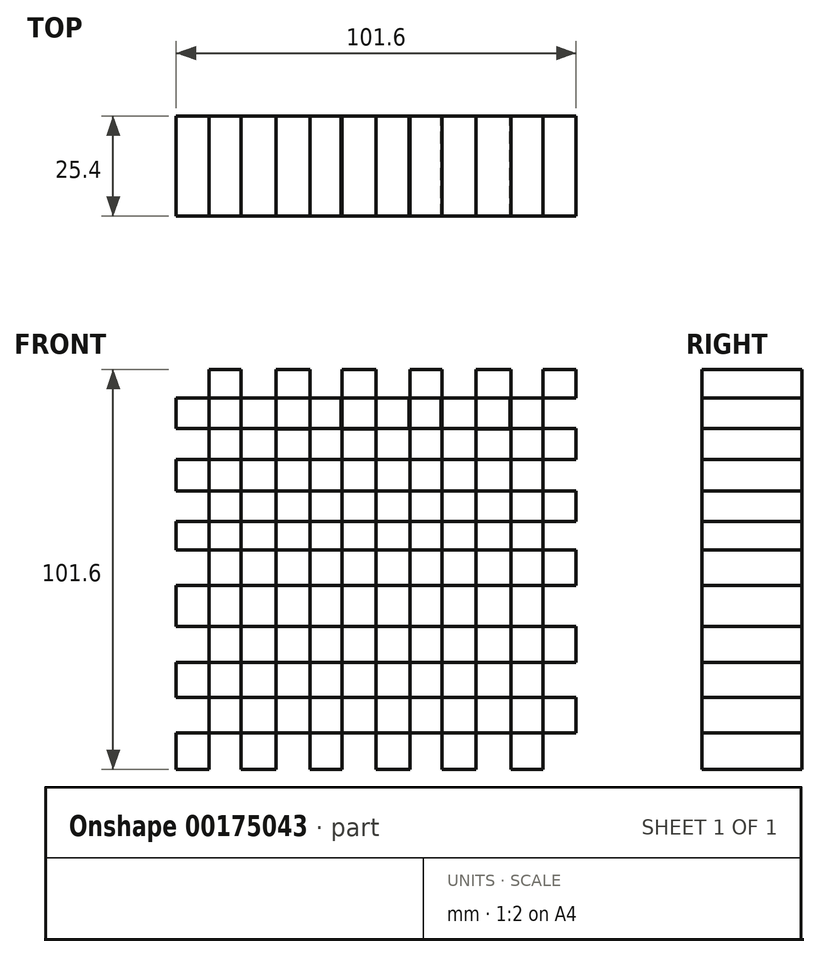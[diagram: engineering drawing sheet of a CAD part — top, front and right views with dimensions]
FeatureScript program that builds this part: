
annotation { "Feature Type Name" : "Feature", "Feature Type Description" : "" }
export const myFeature = defineFeature(function(context is Context, id is Id, definition is map)
    precondition{}
    {
        {
            var Q0;
            Q0=qCreatedBy(makeId("Front.planeOp"),FACE);
            var sketch = newSketch(context, id + "F0", { "sketchPlane" : qUnion([Q0])});
            skLineSegment(sketch, "E0.bottom", {"start": v(-50.8, 45.86) * mm, "end": v(0, 45.86) * mm});
            skLineSegment(sketch, "E0.top", {"start": v(-50.8, -55.74) * mm, "end": v(0, -55.74) * mm});
            skLineSegment(sketch, "E0.left", {"start": v(-50.8, 45.86) * mm, "end": v(-50.8, -55.74) * mm});
            skLineSegment(sketch, "E1", {"start": v(0, 45.86) * mm, "end": v(0, -55.74) * mm});
            skLineSegment(sketch, "E2", {"start": v(-34.3, 45.86) * mm, "end": v(-34.3, -55.74) * mm});
            skLineSegment(sketch, "E3", {"start": v(-16.76, 45.86) * mm, "end": v(-16.76, -55.74) * mm});
            skLineSegment(sketch, "E4", {"start": v(-25.4, 45.86) * mm, "end": v(-25.4, -55.74) * mm});
            skLineSegment(sketch, "E5", {"start": v(-42.42, 45.86) * mm, "end": v(-42.42, -55.74) * mm});
            skLineSegment(sketch, "E6", {"start": v(-8.64, 45.86) * mm, "end": v(-8.64, -55.74) * mm});
            skLineSegment(sketch, "E7", {"start": v(0, 0) * mm, "end": v(-50.8, 0) * mm});
            skLineSegment(sketch, "E8", {"start": v(-50.8, 23.07) * mm, "end": v(0, 23.07) * mm});
            skLineSegment(sketch, "E9", {"start": v(-50.8, -28.57) * mm, "end": v(0, -28.57) * mm});
            skLineSegment(sketch, "E10", {"start": v(-50.8, -9.03) * mm, "end": v(0, -9.03) * mm});
            skLineSegment(sketch, "E11", {"start": v(-50.8, -46.5) * mm, "end": v(0, -46.5) * mm});
            skLineSegment(sketch, "E12", {"start": v(-50.8, 30.83) * mm, "end": v(0, 30.83) * mm});
            skLineSegment(sketch, "E13", {"start": v(-50.8, 38.59) * mm, "end": v(0, 38.59) * mm});
            skLineSegment(sketch, "E14", {"start": v(-50.8, 15.04) * mm, "end": v(0, 15.04) * mm});
            skLineSegment(sketch, "E15", {"start": v(-50.8, 7.29) * mm, "end": v(0, 7.29) * mm});
            skLineSegment(sketch, "E16", {"start": v(-50.8, -19.47) * mm, "end": v(0, -19.47) * mm});
            skLineSegment(sketch, "E17", {"start": v(-50.8, -37.4) * mm, "end": v(0, -37.4) * mm});
            skLineSegment(sketch, "E18.MirrorCS", {"start": v(50.8, 45.86) * mm, "end": v(0, 45.86) * mm});
            skLineSegment(sketch, "E19.MirrorCS", {"start": v(50.8, 45.86) * mm, "end": v(50.8, -55.74) * mm});
            skLineSegment(sketch, "E20.MirrorCS", {"start": v(50.8, -55.74) * mm, "end": v(0, -55.74) * mm});
            skLineSegment(sketch, "E21.MirrorCS", {"start": v(42.42, 45.86) * mm, "end": v(42.42, -55.74) * mm});
            skLineSegment(sketch, "E22.MirrorCS", {"start": v(34.3, 45.86) * mm, "end": v(34.3, -55.74) * mm});
            skLineSegment(sketch, "E23.MirrorCS", {"start": v(25.4, 45.86) * mm, "end": v(25.4, -55.74) * mm});
            skLineSegment(sketch, "E24.MirrorCS", {"start": v(16.76, 45.86) * mm, "end": v(16.76, -55.74) * mm});
            skLineSegment(sketch, "E25.MirrorCS", {"start": v(8.64, 45.86) * mm, "end": v(8.64, -55.74) * mm});
            skLineSegment(sketch, "E26.MirrorCS", {"start": v(50.8, 38.59) * mm, "end": v(0, 38.59) * mm});
            skLineSegment(sketch, "E27.MirrorCS", {"start": v(50.8, 30.83) * mm, "end": v(0, 30.83) * mm});
            skLineSegment(sketch, "E28.MirrorCS", {"start": v(50.8, 23.07) * mm, "end": v(0, 23.07) * mm});
            skLineSegment(sketch, "E29.MirrorCS", {"start": v(50.8, 15.04) * mm, "end": v(0, 15.04) * mm});
            skLineSegment(sketch, "E30.MirrorCS", {"start": v(50.8, 7.29) * mm, "end": v(0, 7.29) * mm});
            skLineSegment(sketch, "E31.MirrorCS", {"start": v(0, 0) * mm, "end": v(50.8, 0) * mm});
            skLineSegment(sketch, "E32.MirrorCS", {"start": v(50.8, -9.03) * mm, "end": v(0, -9.03) * mm});
            skLineSegment(sketch, "E33.MirrorCS", {"start": v(50.8, -19.47) * mm, "end": v(0, -19.47) * mm});
            skLineSegment(sketch, "E34.MirrorCS", {"start": v(50.8, -28.57) * mm, "end": v(0, -28.57) * mm});
            skLineSegment(sketch, "E35.MirrorCS", {"start": v(50.8, -37.4) * mm, "end": v(0, -37.4) * mm});
            skLineSegment(sketch, "E36.MirrorCS", {"start": v(50.8, -46.5) * mm, "end": v(0, -46.5) * mm});
            skSolve(sketch);
        }
        {
            var Q0;
            {var subQ0=sQuery(id+"F0.wireOp",EDGE,"E0.left");var subQ1=sQuery(id+"F0.wireOp",EDGE,"E0.top");var subQ2=makeQuery(id+"F0.imprint","INTERSECT",VERTEX,{"derivedFrom":[subQ1,subQ0]});Q0=makeQuery(id+"F0.imprint","IMPRINT",FACE,{"disambiguationData":[TD([[makeQuery(id+"F0.imprint","IMPRINT",EDGE,{"disambiguationData":[TD([[subQ2,-1.0]])],"derivedFrom":subQ1}),1.0]])]});}
            var Q1;
            {var subQ0=sQuery(id+"F0.wireOp",EDGE,"E19.MirrorCS");var subQ1=sQuery(id+"F0.wireOp",EDGE,"E18.MirrorCS");var subQ2=makeQuery(id+"F0.imprint","INTERSECT",VERTEX,{"derivedFrom":[subQ1,subQ0]});Q1=makeQuery(id+"F0.imprint","IMPRINT",FACE,{"disambiguationData":[TD([[makeQuery(id+"F0.imprint","IMPRINT",EDGE,{"disambiguationData":[TD([[subQ2,-1.0]])],"derivedFrom":subQ1}),1.0]])]});}
            var Q2;
            {var subQ0=sQuery(id+"F0.wireOp",EDGE,"E2");var subQ1=sQuery(id+"F0.wireOp",EDGE,"E0.bottom");var subQ2=makeQuery(id+"F0.imprint","INTERSECT",VERTEX,{"derivedFrom":[subQ1,subQ0]});Q2=makeQuery(id+"F0.imprint","IMPRINT",FACE,{"disambiguationData":[TD([[makeQuery(id+"F0.imprint","IMPRINT",EDGE,{"disambiguationData":[TD([[subQ2,1.0]])],"derivedFrom":subQ1}),-1.0]])]});}
            var Q3;
            {var subQ0=sQuery(id+"F0.wireOp",EDGE,"E3");var subQ1=sQuery(id+"F0.wireOp",EDGE,"E0.bottom");var subQ2=makeQuery(id+"F0.imprint","INTERSECT",VERTEX,{"derivedFrom":[subQ1,subQ0]});Q3=makeQuery(id+"F0.imprint","IMPRINT",FACE,{"disambiguationData":[TD([[makeQuery(id+"F0.imprint","IMPRINT",EDGE,{"disambiguationData":[TD([[subQ2,1.0]])],"derivedFrom":subQ1}),-1.0]])]});}
            var Q4;
            {var subQ1=sQuery(id+"F0.wireOp",EDGE,"E0.bottom");var subQ3=sQuery(id+"F0.wireOp",EDGE,"E6");var subQ4=makeQuery(id+"F0.imprint","INTERSECT",VERTEX,{"derivedFrom":[subQ1,subQ3]});Q4=makeQuery(id+"F0.imprint","IMPRINT",FACE,{"disambiguationData":[TD([[makeQuery(id+"F0.imprint","IMPRINT",EDGE,{"disambiguationData":[TD([[subQ4,-1.0]])],"derivedFrom":subQ3}),1.0]])]});}
            var Q5;
            {var subQ0=sQuery(id+"F0.wireOp",EDGE,"E2");var subQ1=sQuery(id+"F0.wireOp",EDGE,"E0.top");var subQ2=makeQuery(id+"F0.imprint","INTERSECT",VERTEX,{"derivedFrom":[subQ1,subQ0]});Q5=makeQuery(id+"F0.imprint","IMPRINT",FACE,{"disambiguationData":[TD([[makeQuery(id+"F0.imprint","IMPRINT",EDGE,{"disambiguationData":[TD([[subQ2,-1.0]])],"derivedFrom":subQ1}),1.0]])]});}
            var Q6;
            {var subQ0=sQuery(id+"F0.wireOp",EDGE,"E3");var subQ1=sQuery(id+"F0.wireOp",EDGE,"E0.top");var subQ2=makeQuery(id+"F0.imprint","INTERSECT",VERTEX,{"derivedFrom":[subQ1,subQ0]});Q6=makeQuery(id+"F0.imprint","IMPRINT",FACE,{"disambiguationData":[TD([[makeQuery(id+"F0.imprint","IMPRINT",EDGE,{"disambiguationData":[TD([[subQ2,-1.0]])],"derivedFrom":subQ1}),1.0]])]});}
            var Q7;
            {var subQ0=sQuery(id+"F0.wireOp",EDGE,"E12");var subQ1=sQuery(id+"F0.wireOp",EDGE,"E0.left");var subQ2=makeQuery(id+"F0.imprint","INTERSECT",VERTEX,{"derivedFrom":[subQ1,subQ0]});Q7=makeQuery(id+"F0.imprint","IMPRINT",FACE,{"disambiguationData":[TD([[makeQuery(id+"F0.imprint","IMPRINT",EDGE,{"disambiguationData":[TD([[subQ2,1.0]])],"derivedFrom":subQ1}),1.0]])]});}
            var Q8;
            {var subQ0=sQuery(id+"F0.wireOp",EDGE,"E8");var subQ1=sQuery(id+"F0.wireOp",EDGE,"E0.left");var subQ2=makeQuery(id+"F0.imprint","INTERSECT",VERTEX,{"derivedFrom":[subQ1,subQ0]});Q8=makeQuery(id+"F0.imprint","IMPRINT",FACE,{"disambiguationData":[TD([[makeQuery(id+"F0.imprint","IMPRINT",EDGE,{"disambiguationData":[TD([[subQ2,-1.0]])],"derivedFrom":subQ1}),1.0]])]});}
            var Q9;
            {var subQ0=sQuery(id+"F0.wireOp",EDGE,"E7");var subQ1=sQuery(id+"F0.wireOp",EDGE,"E0.left");var subQ2=makeQuery(id+"F0.imprint","INTERSECT",VERTEX,{"derivedFrom":[subQ1,subQ0]});Q9=makeQuery(id+"F0.imprint","IMPRINT",FACE,{"disambiguationData":[TD([[makeQuery(id+"F0.imprint","IMPRINT",EDGE,{"disambiguationData":[TD([[subQ2,1.0]])],"derivedFrom":subQ1}),1.0]])]});}
            var Q10;
            {var subQ0=sQuery(id+"F0.wireOp",EDGE,"E10");var subQ1=sQuery(id+"F0.wireOp",EDGE,"E0.left");var subQ2=makeQuery(id+"F0.imprint","INTERSECT",VERTEX,{"derivedFrom":[subQ1,subQ0]});Q10=makeQuery(id+"F0.imprint","IMPRINT",FACE,{"disambiguationData":[TD([[makeQuery(id+"F0.imprint","IMPRINT",EDGE,{"disambiguationData":[TD([[subQ2,-1.0]])],"derivedFrom":subQ1}),1.0]])]});}
            var Q11;
            {var subQ0=sQuery(id+"F0.wireOp",EDGE,"E9");var subQ1=sQuery(id+"F0.wireOp",EDGE,"E0.left");var subQ2=makeQuery(id+"F0.imprint","INTERSECT",VERTEX,{"derivedFrom":[subQ1,subQ0]});Q11=makeQuery(id+"F0.imprint","IMPRINT",FACE,{"disambiguationData":[TD([[makeQuery(id+"F0.imprint","IMPRINT",EDGE,{"disambiguationData":[TD([[subQ2,-1.0]])],"derivedFrom":subQ1}),1.0]])]});}
            var Q12;
            {var subQ0=sQuery(id+"F0.wireOp",EDGE,"E20.MirrorCS");var subQ5=sQuery(id+"F0.wireOp",EDGE,"E25.MirrorCS");var subQ6=makeQuery(id+"F0.imprint","INTERSECT",VERTEX,{"derivedFrom":[subQ5,subQ0]});Q12=makeQuery(id+"F0.imprint","IMPRINT",FACE,{"disambiguationData":[TD([[makeQuery(id+"F0.imprint","IMPRINT",EDGE,{"disambiguationData":[TD([[subQ6,1.0]])],"derivedFrom":subQ5}),-1.0]])]});}
            var Q13;
            {var subQ0=sQuery(id+"F0.wireOp",EDGE,"E22.MirrorCS");var subQ1=sQuery(id+"F0.wireOp",EDGE,"E18.MirrorCS");var subQ2=makeQuery(id+"F0.imprint","INTERSECT",VERTEX,{"derivedFrom":[subQ1,subQ0]});Q13=makeQuery(id+"F0.imprint","IMPRINT",FACE,{"disambiguationData":[TD([[makeQuery(id+"F0.imprint","IMPRINT",EDGE,{"disambiguationData":[TD([[subQ2,-1.0]])],"derivedFrom":subQ1}),1.0]])]});}
            var Q14;
            {var subQ0=sQuery(id+"F0.wireOp",EDGE,"E24.MirrorCS");var subQ1=sQuery(id+"F0.wireOp",EDGE,"E18.MirrorCS");var subQ2=makeQuery(id+"F0.imprint","INTERSECT",VERTEX,{"derivedFrom":[subQ1,subQ0]});Q14=makeQuery(id+"F0.imprint","IMPRINT",FACE,{"disambiguationData":[TD([[makeQuery(id+"F0.imprint","IMPRINT",EDGE,{"disambiguationData":[TD([[subQ2,-1.0]])],"derivedFrom":subQ1}),1.0]])]});}
            var Q15;
            {var subQ0=sQuery(id+"F0.wireOp",EDGE,"E27.MirrorCS");var subQ1=sQuery(id+"F0.wireOp",EDGE,"E19.MirrorCS");var subQ2=makeQuery(id+"F0.imprint","INTERSECT",VERTEX,{"derivedFrom":[subQ1,subQ0]});Q15=makeQuery(id+"F0.imprint","IMPRINT",FACE,{"disambiguationData":[TD([[makeQuery(id+"F0.imprint","IMPRINT",EDGE,{"disambiguationData":[TD([[subQ2,-1.0]])],"derivedFrom":subQ1}),-1.0]])]});}
            var Q16;
            {var subQ0=sQuery(id+"F0.wireOp",EDGE,"E29.MirrorCS");var subQ1=sQuery(id+"F0.wireOp",EDGE,"E19.MirrorCS");var subQ2=makeQuery(id+"F0.imprint","INTERSECT",VERTEX,{"derivedFrom":[subQ1,subQ0]});Q16=makeQuery(id+"F0.imprint","IMPRINT",FACE,{"disambiguationData":[TD([[makeQuery(id+"F0.imprint","IMPRINT",EDGE,{"disambiguationData":[TD([[subQ2,-1.0]])],"derivedFrom":subQ1}),-1.0]])]});}
            var Q17;
            {var subQ0=sQuery(id+"F0.wireOp",EDGE,"E31.MirrorCS");var subQ1=sQuery(id+"F0.wireOp",EDGE,"E19.MirrorCS");var subQ2=makeQuery(id+"F0.imprint","INTERSECT",VERTEX,{"derivedFrom":[subQ1,subQ0]});Q17=makeQuery(id+"F0.imprint","IMPRINT",FACE,{"disambiguationData":[TD([[makeQuery(id+"F0.imprint","IMPRINT",EDGE,{"disambiguationData":[TD([[subQ2,-1.0]])],"derivedFrom":subQ1}),-1.0]])]});}
            var Q18;
            {var subQ0=sQuery(id+"F0.wireOp",EDGE,"E33.MirrorCS");var subQ1=sQuery(id+"F0.wireOp",EDGE,"E19.MirrorCS");var subQ2=makeQuery(id+"F0.imprint","INTERSECT",VERTEX,{"derivedFrom":[subQ1,subQ0]});Q18=makeQuery(id+"F0.imprint","IMPRINT",FACE,{"disambiguationData":[TD([[makeQuery(id+"F0.imprint","IMPRINT",EDGE,{"disambiguationData":[TD([[subQ2,-1.0]])],"derivedFrom":subQ1}),-1.0]])]});}
            var Q19;
            {var subQ0=sQuery(id+"F0.wireOp",EDGE,"E35.MirrorCS");var subQ1=sQuery(id+"F0.wireOp",EDGE,"E19.MirrorCS");var subQ2=makeQuery(id+"F0.imprint","INTERSECT",VERTEX,{"derivedFrom":[subQ1,subQ0]});Q19=makeQuery(id+"F0.imprint","IMPRINT",FACE,{"disambiguationData":[TD([[makeQuery(id+"F0.imprint","IMPRINT",EDGE,{"disambiguationData":[TD([[subQ2,-1.0]])],"derivedFrom":subQ1}),-1.0]])]});}
            var Q20;
            {var subQ0=sQuery(id+"F0.wireOp",EDGE,"E20.MirrorCS");var subQ1=sQuery(id+"F0.wireOp",EDGE,"E21.MirrorCS");var subQ2=makeQuery(id+"F0.imprint","INTERSECT",VERTEX,{"derivedFrom":[subQ1,subQ0]});Q20=makeQuery(id+"F0.imprint","IMPRINT",FACE,{"disambiguationData":[TD([[makeQuery(id+"F0.imprint","IMPRINT",EDGE,{"disambiguationData":[TD([[subQ2,1.0]])],"derivedFrom":subQ1}),-1.0]])]});}
            var Q21;
            {var subQ0=sQuery(id+"F0.wireOp",EDGE,"E20.MirrorCS");var subQ1=sQuery(id+"F0.wireOp",EDGE,"E23.MirrorCS");var subQ2=makeQuery(id+"F0.imprint","INTERSECT",VERTEX,{"derivedFrom":[subQ1,subQ0]});Q21=makeQuery(id+"F0.imprint","IMPRINT",FACE,{"disambiguationData":[TD([[makeQuery(id+"F0.imprint","IMPRINT",EDGE,{"disambiguationData":[TD([[subQ2,1.0]])],"derivedFrom":subQ1}),-1.0]])]});}
            var Q22;
            {var subQ0=sQuery(id+"F0.wireOp",EDGE,"E13");var subQ1=sQuery(id+"F0.wireOp",EDGE,"E2");var subQ2=makeQuery(id+"F0.imprint","INTERSECT",VERTEX,{"derivedFrom":[subQ1,subQ0]});Q22=makeQuery(id+"F0.imprint","IMPRINT",FACE,{"disambiguationData":[TD([[makeQuery(id+"F0.imprint","IMPRINT",EDGE,{"disambiguationData":[TD([[subQ2,-1.0]])],"derivedFrom":subQ1}),1.0]])]});}
            var Q23;
            {var subQ0=sQuery(id+"F0.wireOp",EDGE,"E8");var subQ1=sQuery(id+"F0.wireOp",EDGE,"E3");var subQ2=makeQuery(id+"F0.imprint","INTERSECT",VERTEX,{"derivedFrom":[subQ1,subQ0]});Q23=makeQuery(id+"F0.imprint","IMPRINT",FACE,{"disambiguationData":[TD([[makeQuery(id+"F0.imprint","IMPRINT",EDGE,{"disambiguationData":[TD([[subQ2,-1.0]])],"derivedFrom":subQ1}),1.0]])]});}
            var Q24;
            {var subQ0=sQuery(id+"F0.wireOp",EDGE,"E9");var subQ1=sQuery(id+"F0.wireOp",EDGE,"E2");var subQ2=makeQuery(id+"F0.imprint","INTERSECT",VERTEX,{"derivedFrom":[subQ1,subQ0]});Q24=makeQuery(id+"F0.imprint","IMPRINT",FACE,{"disambiguationData":[TD([[makeQuery(id+"F0.imprint","IMPRINT",EDGE,{"disambiguationData":[TD([[subQ2,-1.0]])],"derivedFrom":subQ1}),1.0]])]});}
            var Q25;
            {var subQ0=sQuery(id+"F0.wireOp",EDGE,"E10");var subQ1=sQuery(id+"F0.wireOp",EDGE,"E2");var subQ2=makeQuery(id+"F0.imprint","INTERSECT",VERTEX,{"derivedFrom":[subQ1,subQ0]});Q25=makeQuery(id+"F0.imprint","IMPRINT",FACE,{"disambiguationData":[TD([[makeQuery(id+"F0.imprint","IMPRINT",EDGE,{"disambiguationData":[TD([[subQ2,-1.0]])],"derivedFrom":subQ1}),1.0]])]});}
            var Q26;
            {var subQ0=sQuery(id+"F0.wireOp",EDGE,"E9");var subQ1=sQuery(id+"F0.wireOp",EDGE,"E3");var subQ2=makeQuery(id+"F0.imprint","INTERSECT",VERTEX,{"derivedFrom":[subQ1,subQ0]});Q26=makeQuery(id+"F0.imprint","IMPRINT",FACE,{"disambiguationData":[TD([[makeQuery(id+"F0.imprint","IMPRINT",EDGE,{"disambiguationData":[TD([[subQ2,-1.0]])],"derivedFrom":subQ1}),1.0]])]});}
            var Q27;
            {var subQ0=sQuery(id+"F0.wireOp",EDGE,"E10");var subQ1=sQuery(id+"F0.wireOp",EDGE,"E3");var subQ2=makeQuery(id+"F0.imprint","INTERSECT",VERTEX,{"derivedFrom":[subQ1,subQ0]});Q27=makeQuery(id+"F0.imprint","IMPRINT",FACE,{"disambiguationData":[TD([[makeQuery(id+"F0.imprint","IMPRINT",EDGE,{"disambiguationData":[TD([[subQ2,-1.0]])],"derivedFrom":subQ1}),1.0]])]});}
            var Q28;
            {var subQ0=sQuery(id+"F0.wireOp",EDGE,"E16");var subQ1=sQuery(id+"F0.wireOp",EDGE,"E3");var subQ2=makeQuery(id+"F0.imprint","INTERSECT",VERTEX,{"derivedFrom":[subQ1,subQ0]});Q28=makeQuery(id+"F0.imprint","IMPRINT",FACE,{"disambiguationData":[TD([[makeQuery(id+"F0.imprint","IMPRINT",EDGE,{"disambiguationData":[TD([[subQ2,-1.0]])],"derivedFrom":subQ1}),-1.0]])]});}
            var Q29;
            {var subQ0=sQuery(id+"F0.wireOp",EDGE,"E8");var subQ1=sQuery(id+"F0.wireOp",EDGE,"E2");var subQ2=makeQuery(id+"F0.imprint","INTERSECT",VERTEX,{"derivedFrom":[subQ1,subQ0]});Q29=makeQuery(id+"F0.imprint","IMPRINT",FACE,{"disambiguationData":[TD([[makeQuery(id+"F0.imprint","IMPRINT",EDGE,{"disambiguationData":[TD([[subQ2,-1.0]])],"derivedFrom":subQ1}),1.0]])]});}
            var Q30;
            {var subQ0=sQuery(id+"F0.wireOp",EDGE,"E15");var subQ1=sQuery(id+"F0.wireOp",EDGE,"E2");var subQ2=makeQuery(id+"F0.imprint","INTERSECT",VERTEX,{"derivedFrom":[subQ1,subQ0]});Q30=makeQuery(id+"F0.imprint","IMPRINT",FACE,{"disambiguationData":[TD([[makeQuery(id+"F0.imprint","IMPRINT",EDGE,{"disambiguationData":[TD([[subQ2,-1.0]])],"derivedFrom":subQ1}),1.0]])]});}
            var Q31;
            {var subQ0=sQuery(id+"F0.wireOp",EDGE,"E12");var subQ1=sQuery(id+"F0.wireOp",EDGE,"E3");var subQ2=makeQuery(id+"F0.imprint","INTERSECT",VERTEX,{"derivedFrom":[subQ1,subQ0]});Q31=makeQuery(id+"F0.imprint","IMPRINT",FACE,{"disambiguationData":[TD([[makeQuery(id+"F0.imprint","IMPRINT",EDGE,{"disambiguationData":[TD([[subQ2,-1.0]])],"derivedFrom":subQ1}),-1.0]])]});}
            var Q32;
            {var subQ0=sQuery(id+"F0.wireOp",EDGE,"E7");var subQ5=sQuery(id+"F0.wireOp",EDGE,"E6");var subQ6=makeQuery(id+"F0.imprint","INTERSECT",VERTEX,{"derivedFrom":[subQ5,subQ0]});Q32=makeQuery(id+"F0.imprint","IMPRINT",FACE,{"disambiguationData":[TD([[makeQuery(id+"F0.imprint","IMPRINT",EDGE,{"disambiguationData":[TD([[subQ6,-1.0]])],"derivedFrom":subQ5}),1.0]])]});}
            var Q33;
            {var subQ0=sQuery(id+"F0.wireOp",EDGE,"E29.MirrorCS");var subQ1=sQuery(id+"F0.wireOp",EDGE,"E22.MirrorCS");var subQ2=makeQuery(id+"F0.imprint","INTERSECT",VERTEX,{"derivedFrom":[subQ1,subQ0]});Q33=makeQuery(id+"F0.imprint","IMPRINT",FACE,{"disambiguationData":[TD([[makeQuery(id+"F0.imprint","IMPRINT",EDGE,{"disambiguationData":[TD([[subQ2,-1.0]])],"derivedFrom":subQ1}),-1.0]])]});}
            var Q34;
            {var subQ0=sQuery(id+"F0.wireOp",EDGE,"E28.MirrorCS");var subQ1=sQuery(id+"F0.wireOp",EDGE,"E23.MirrorCS");var subQ2=makeQuery(id+"F0.imprint","INTERSECT",VERTEX,{"derivedFrom":[subQ1,subQ0]});Q34=makeQuery(id+"F0.imprint","IMPRINT",FACE,{"disambiguationData":[TD([[makeQuery(id+"F0.imprint","IMPRINT",EDGE,{"disambiguationData":[TD([[subQ2,-1.0]])],"derivedFrom":subQ1}),-1.0]])]});}
            var Q35;
            {var subQ0=sQuery(id+"F0.wireOp",EDGE,"E7");var subQ1=sQuery(id+"F0.wireOp",EDGE,"E3");var subQ2=makeQuery(id+"F0.imprint","INTERSECT",VERTEX,{"derivedFrom":[subQ1,subQ0]});Q35=makeQuery(id+"F0.imprint","IMPRINT",FACE,{"disambiguationData":[TD([[makeQuery(id+"F0.imprint","IMPRINT",EDGE,{"disambiguationData":[TD([[subQ2,-1.0]])],"derivedFrom":subQ1}),-1.0]])]});}
            var Q36;
            {var subQ0=sQuery(id+"F0.wireOp",EDGE,"E30.MirrorCS");var subQ1=sQuery(id+"F0.wireOp",EDGE,"E23.MirrorCS");var subQ2=makeQuery(id+"F0.imprint","INTERSECT",VERTEX,{"derivedFrom":[subQ1,subQ0]});Q36=makeQuery(id+"F0.imprint","IMPRINT",FACE,{"disambiguationData":[TD([[makeQuery(id+"F0.imprint","IMPRINT",EDGE,{"disambiguationData":[TD([[subQ2,-1.0]])],"derivedFrom":subQ1}),-1.0]])]});}
            var Q37;
            {var subQ0=sQuery(id+"F0.wireOp",EDGE,"E27.MirrorCS");var subQ1=sQuery(id+"F0.wireOp",EDGE,"E24.MirrorCS");var subQ2=makeQuery(id+"F0.imprint","INTERSECT",VERTEX,{"derivedFrom":[subQ1,subQ0]});Q37=makeQuery(id+"F0.imprint","IMPRINT",FACE,{"disambiguationData":[TD([[makeQuery(id+"F0.imprint","IMPRINT",EDGE,{"disambiguationData":[TD([[subQ2,-1.0]])],"derivedFrom":subQ1}),-1.0]])]});}
            var Q38;
            {var subQ3=sQuery(id+"F0.wireOp",EDGE,"E30.MirrorCS");var subQ5=sQuery(id+"F0.wireOp",EDGE,"E25.MirrorCS");var subQ6=makeQuery(id+"F0.imprint","INTERSECT",VERTEX,{"derivedFrom":[subQ5,subQ3]});Q38=makeQuery(id+"F0.imprint","IMPRINT",FACE,{"disambiguationData":[TD([[makeQuery(id+"F0.imprint","IMPRINT",EDGE,{"disambiguationData":[TD([[subQ6,-1.0]])],"derivedFrom":subQ5}),-1.0]])]});}
            var Q39;
            {var subQ3=sQuery(id+"F0.wireOp",EDGE,"E12");var subQ5=sQuery(id+"F0.wireOp",EDGE,"E6");var subQ6=makeQuery(id+"F0.imprint","INTERSECT",VERTEX,{"derivedFrom":[subQ5,subQ3]});Q39=makeQuery(id+"F0.imprint","IMPRINT",FACE,{"disambiguationData":[TD([[makeQuery(id+"F0.imprint","IMPRINT",EDGE,{"disambiguationData":[TD([[subQ6,-1.0]])],"derivedFrom":subQ5}),1.0]])]});}
            var Q40;
            {var subQ0=sQuery(id+"F0.wireOp",EDGE,"E31.MirrorCS");var subQ1=sQuery(id+"F0.wireOp",EDGE,"E24.MirrorCS");var subQ2=makeQuery(id+"F0.imprint","INTERSECT",VERTEX,{"derivedFrom":[subQ1,subQ0]});Q40=makeQuery(id+"F0.imprint","IMPRINT",FACE,{"disambiguationData":[TD([[makeQuery(id+"F0.imprint","IMPRINT",EDGE,{"disambiguationData":[TD([[subQ2,-1.0]])],"derivedFrom":subQ1}),-1.0]])]});}
            var Q41;
            {var subQ0=sQuery(id+"F0.wireOp",EDGE,"E31.MirrorCS");var subQ1=sQuery(id+"F0.wireOp",EDGE,"E22.MirrorCS");var subQ2=makeQuery(id+"F0.imprint","INTERSECT",VERTEX,{"derivedFrom":[subQ1,subQ0]});Q41=makeQuery(id+"F0.imprint","IMPRINT",FACE,{"disambiguationData":[TD([[makeQuery(id+"F0.imprint","IMPRINT",EDGE,{"disambiguationData":[TD([[subQ2,-1.0]])],"derivedFrom":subQ1}),-1.0]])]});}
            var Q42;
            {var subQ0=sQuery(id+"F0.wireOp",EDGE,"E7");var subQ1=sQuery(id+"F0.wireOp",EDGE,"E2");var subQ2=makeQuery(id+"F0.imprint","INTERSECT",VERTEX,{"derivedFrom":[subQ1,subQ0]});Q42=makeQuery(id+"F0.imprint","IMPRINT",FACE,{"disambiguationData":[TD([[makeQuery(id+"F0.imprint","IMPRINT",EDGE,{"disambiguationData":[TD([[subQ2,-1.0]])],"derivedFrom":subQ1}),-1.0]])]});}
            var Q43;
            {var subQ0=sQuery(id+"F0.wireOp",EDGE,"E14");var subQ1=sQuery(id+"F0.wireOp",EDGE,"E2");var subQ2=makeQuery(id+"F0.imprint","INTERSECT",VERTEX,{"derivedFrom":[subQ1,subQ0]});Q43=makeQuery(id+"F0.imprint","IMPRINT",FACE,{"disambiguationData":[TD([[makeQuery(id+"F0.imprint","IMPRINT",EDGE,{"disambiguationData":[TD([[subQ2,-1.0]])],"derivedFrom":subQ1}),-1.0]])]});}
            var Q44;
            {var subQ0=sQuery(id+"F0.wireOp",EDGE,"E28.MirrorCS");var subQ5=sQuery(id+"F0.wireOp",EDGE,"E25.MirrorCS");var subQ6=makeQuery(id+"F0.imprint","INTERSECT",VERTEX,{"derivedFrom":[subQ5,subQ0]});Q44=makeQuery(id+"F0.imprint","IMPRINT",FACE,{"disambiguationData":[TD([[makeQuery(id+"F0.imprint","IMPRINT",EDGE,{"disambiguationData":[TD([[subQ6,-1.0]])],"derivedFrom":subQ5}),-1.0]])]});}
            var Q45;
            {var subQ0=sQuery(id+"F0.wireOp",EDGE,"E34.MirrorCS");var subQ1=sQuery(id+"F0.wireOp",EDGE,"E23.MirrorCS");var subQ2=makeQuery(id+"F0.imprint","INTERSECT",VERTEX,{"derivedFrom":[subQ1,subQ0]});Q45=makeQuery(id+"F0.imprint","IMPRINT",FACE,{"disambiguationData":[TD([[makeQuery(id+"F0.imprint","IMPRINT",EDGE,{"disambiguationData":[TD([[subQ2,-1.0]])],"derivedFrom":subQ1}),-1.0]])]});}
            var Q46;
            {var subQ0=sQuery(id+"F0.wireOp",EDGE,"E15");var subQ1=sQuery(id+"F0.wireOp",EDGE,"E3");var subQ2=makeQuery(id+"F0.imprint","INTERSECT",VERTEX,{"derivedFrom":[subQ1,subQ0]});Q46=makeQuery(id+"F0.imprint","IMPRINT",FACE,{"disambiguationData":[TD([[makeQuery(id+"F0.imprint","IMPRINT",EDGE,{"disambiguationData":[TD([[subQ2,-1.0]])],"derivedFrom":subQ1}),1.0]])]});}
            var Q47;
            {var subQ0=sQuery(id+"F0.wireOp",EDGE,"E33.MirrorCS");var subQ1=sQuery(id+"F0.wireOp",EDGE,"E24.MirrorCS");var subQ2=makeQuery(id+"F0.imprint","INTERSECT",VERTEX,{"derivedFrom":[subQ1,subQ0]});Q47=makeQuery(id+"F0.imprint","IMPRINT",FACE,{"disambiguationData":[TD([[makeQuery(id+"F0.imprint","IMPRINT",EDGE,{"disambiguationData":[TD([[subQ2,-1.0]])],"derivedFrom":subQ1}),-1.0]])]});}
            var Q48;
            {var subQ0=sQuery(id+"F0.wireOp",EDGE,"E14");var subQ5=sQuery(id+"F0.wireOp",EDGE,"E6");var subQ6=makeQuery(id+"F0.imprint","INTERSECT",VERTEX,{"derivedFrom":[subQ5,subQ0]});Q48=makeQuery(id+"F0.imprint","IMPRINT",FACE,{"disambiguationData":[TD([[makeQuery(id+"F0.imprint","IMPRINT",EDGE,{"disambiguationData":[TD([[subQ6,-1.0]])],"derivedFrom":subQ5}),1.0]])]});}
            var Q49;
            {var subQ0=sQuery(id+"F0.wireOp",EDGE,"E32.MirrorCS");var subQ1=sQuery(id+"F0.wireOp",EDGE,"E23.MirrorCS");var subQ2=makeQuery(id+"F0.imprint","INTERSECT",VERTEX,{"derivedFrom":[subQ1,subQ0]});Q49=makeQuery(id+"F0.imprint","IMPRINT",FACE,{"disambiguationData":[TD([[makeQuery(id+"F0.imprint","IMPRINT",EDGE,{"disambiguationData":[TD([[subQ2,-1.0]])],"derivedFrom":subQ1}),-1.0]])]});}
            var Q50;
            {var subQ0=sQuery(id+"F0.wireOp",EDGE,"E34.MirrorCS");var subQ5=sQuery(id+"F0.wireOp",EDGE,"E25.MirrorCS");var subQ6=makeQuery(id+"F0.imprint","INTERSECT",VERTEX,{"derivedFrom":[subQ5,subQ0]});Q50=makeQuery(id+"F0.imprint","IMPRINT",FACE,{"disambiguationData":[TD([[makeQuery(id+"F0.imprint","IMPRINT",EDGE,{"disambiguationData":[TD([[subQ6,-1.0]])],"derivedFrom":subQ5}),-1.0]])]});}
            var Q51;
            {var subQ0=sQuery(id+"F0.wireOp",EDGE,"E27.MirrorCS");var subQ1=sQuery(id+"F0.wireOp",EDGE,"E22.MirrorCS");var subQ2=makeQuery(id+"F0.imprint","INTERSECT",VERTEX,{"derivedFrom":[subQ1,subQ0]});Q51=makeQuery(id+"F0.imprint","IMPRINT",FACE,{"disambiguationData":[TD([[makeQuery(id+"F0.imprint","IMPRINT",EDGE,{"disambiguationData":[TD([[subQ2,-1.0]])],"derivedFrom":subQ1}),-1.0]])]});}
            var Q52;
            {var subQ0=sQuery(id+"F0.wireOp",EDGE,"E14");var subQ1=sQuery(id+"F0.wireOp",EDGE,"E3");var subQ2=makeQuery(id+"F0.imprint","INTERSECT",VERTEX,{"derivedFrom":[subQ1,subQ0]});Q52=makeQuery(id+"F0.imprint","IMPRINT",FACE,{"disambiguationData":[TD([[makeQuery(id+"F0.imprint","IMPRINT",EDGE,{"disambiguationData":[TD([[subQ2,-1.0]])],"derivedFrom":subQ1}),-1.0]])]});}
            var Q53;
            {var subQ0=sQuery(id+"F0.wireOp",EDGE,"E32.MirrorCS");var subQ5=sQuery(id+"F0.wireOp",EDGE,"E25.MirrorCS");var subQ6=makeQuery(id+"F0.imprint","INTERSECT",VERTEX,{"derivedFrom":[subQ5,subQ0]});Q53=makeQuery(id+"F0.imprint","IMPRINT",FACE,{"disambiguationData":[TD([[makeQuery(id+"F0.imprint","IMPRINT",EDGE,{"disambiguationData":[TD([[subQ6,-1.0]])],"derivedFrom":subQ5}),-1.0]])]});}
            var Q54;
            {var subQ0=sQuery(id+"F0.wireOp",EDGE,"E33.MirrorCS");var subQ1=sQuery(id+"F0.wireOp",EDGE,"E22.MirrorCS");var subQ2=makeQuery(id+"F0.imprint","INTERSECT",VERTEX,{"derivedFrom":[subQ1,subQ0]});Q54=makeQuery(id+"F0.imprint","IMPRINT",FACE,{"disambiguationData":[TD([[makeQuery(id+"F0.imprint","IMPRINT",EDGE,{"disambiguationData":[TD([[subQ2,-1.0]])],"derivedFrom":subQ1}),-1.0]])]});}
            var Q55;
            {var subQ0=sQuery(id+"F0.wireOp",EDGE,"E12");var subQ1=sQuery(id+"F0.wireOp",EDGE,"E2");var subQ2=makeQuery(id+"F0.imprint","INTERSECT",VERTEX,{"derivedFrom":[subQ1,subQ0]});Q55=makeQuery(id+"F0.imprint","IMPRINT",FACE,{"disambiguationData":[TD([[makeQuery(id+"F0.imprint","IMPRINT",EDGE,{"disambiguationData":[TD([[subQ2,-1.0]])],"derivedFrom":subQ1}),-1.0]])]});}
            var Q56;
            {var subQ0=sQuery(id+"F0.wireOp",EDGE,"E16");var subQ1=sQuery(id+"F0.wireOp",EDGE,"E2");var subQ2=makeQuery(id+"F0.imprint","INTERSECT",VERTEX,{"derivedFrom":[subQ1,subQ0]});Q56=makeQuery(id+"F0.imprint","IMPRINT",FACE,{"disambiguationData":[TD([[makeQuery(id+"F0.imprint","IMPRINT",EDGE,{"disambiguationData":[TD([[subQ2,-1.0]])],"derivedFrom":subQ1}),-1.0]])]});}
            var Q57;
            {var subQ3=sQuery(id+"F0.wireOp",EDGE,"E16");var subQ5=sQuery(id+"F0.wireOp",EDGE,"E6");var subQ7=makeQuery(id+"F0.imprint","INTERSECT",VERTEX,{"derivedFrom":[subQ5,subQ3]});Q57=makeQuery(id+"F0.imprint","IMPRINT",FACE,{"disambiguationData":[TD([[makeQuery(id+"F0.imprint","IMPRINT",EDGE,{"disambiguationData":[TD([[subQ7,-1.0]])],"derivedFrom":subQ5}),1.0]])]});}
            var Q58;
            {var subQ0=sQuery(id+"F0.wireOp",EDGE,"E29.MirrorCS");var subQ1=sQuery(id+"F0.wireOp",EDGE,"E24.MirrorCS");var subQ2=makeQuery(id+"F0.imprint","INTERSECT",VERTEX,{"derivedFrom":[subQ1,subQ0]});Q58=makeQuery(id+"F0.imprint","IMPRINT",FACE,{"disambiguationData":[TD([[makeQuery(id+"F0.imprint","IMPRINT",EDGE,{"disambiguationData":[TD([[subQ2,-1.0]])],"derivedFrom":subQ1}),-1.0]])]});}
            var Q59;
            {var subQ0=sQuery(id+"F0.wireOp",EDGE,"E13");var subQ1=sQuery(id+"F0.wireOp",EDGE,"E3");var subQ2=makeQuery(id+"F0.imprint","INTERSECT",VERTEX,{"derivedFrom":[subQ1,subQ0]});Q59=makeQuery(id+"F0.imprint","IMPRINT",FACE,{"disambiguationData":[TD([[makeQuery(id+"F0.imprint","IMPRINT",EDGE,{"disambiguationData":[TD([[subQ2,-1.0]])],"derivedFrom":subQ1}),1.0]])]});}
            var Q60;
            {var subQ3=sQuery(id+"F0.wireOp",EDGE,"E26.MirrorCS");var subQ5=sQuery(id+"F0.wireOp",EDGE,"E25.MirrorCS");var subQ6=makeQuery(id+"F0.imprint","INTERSECT",VERTEX,{"derivedFrom":[subQ5,subQ3]});Q60=makeQuery(id+"F0.imprint","IMPRINT",FACE,{"disambiguationData":[TD([[makeQuery(id+"F0.imprint","IMPRINT",EDGE,{"disambiguationData":[TD([[subQ6,-1.0]])],"derivedFrom":subQ5}),-1.0]])]});}
            var Q61;
            {var subQ0=sQuery(id+"F0.wireOp",EDGE,"E26.MirrorCS");var subQ1=sQuery(id+"F0.wireOp",EDGE,"E23.MirrorCS");var subQ2=makeQuery(id+"F0.imprint","INTERSECT",VERTEX,{"derivedFrom":[subQ1,subQ0]});Q61=makeQuery(id+"F0.imprint","IMPRINT",FACE,{"disambiguationData":[TD([[makeQuery(id+"F0.imprint","IMPRINT",EDGE,{"disambiguationData":[TD([[subQ2,-1.0]])],"derivedFrom":subQ1}),-1.0]])]});}
            var Q62;
            {var subQ0=sQuery(id+"F0.wireOp",EDGE,"E26.MirrorCS");var subQ1=sQuery(id+"F0.wireOp",EDGE,"E21.MirrorCS");var subQ2=makeQuery(id+"F0.imprint","INTERSECT",VERTEX,{"derivedFrom":[subQ1,subQ0]});Q62=makeQuery(id+"F0.imprint","IMPRINT",FACE,{"disambiguationData":[TD([[makeQuery(id+"F0.imprint","IMPRINT",EDGE,{"disambiguationData":[TD([[subQ2,-1.0]])],"derivedFrom":subQ1}),-1.0]])]});}
            var Q63;
            {var subQ0=sQuery(id+"F0.wireOp",EDGE,"E28.MirrorCS");var subQ1=sQuery(id+"F0.wireOp",EDGE,"E21.MirrorCS");var subQ2=makeQuery(id+"F0.imprint","INTERSECT",VERTEX,{"derivedFrom":[subQ1,subQ0]});Q63=makeQuery(id+"F0.imprint","IMPRINT",FACE,{"disambiguationData":[TD([[makeQuery(id+"F0.imprint","IMPRINT",EDGE,{"disambiguationData":[TD([[subQ2,-1.0]])],"derivedFrom":subQ1}),-1.0]])]});}
            var Q64;
            {var subQ0=sQuery(id+"F0.wireOp",EDGE,"E30.MirrorCS");var subQ1=sQuery(id+"F0.wireOp",EDGE,"E21.MirrorCS");var subQ2=makeQuery(id+"F0.imprint","INTERSECT",VERTEX,{"derivedFrom":[subQ1,subQ0]});Q64=makeQuery(id+"F0.imprint","IMPRINT",FACE,{"disambiguationData":[TD([[makeQuery(id+"F0.imprint","IMPRINT",EDGE,{"disambiguationData":[TD([[subQ2,-1.0]])],"derivedFrom":subQ1}),-1.0]])]});}
            var Q65;
            {var subQ0=sQuery(id+"F0.wireOp",EDGE,"E32.MirrorCS");var subQ1=sQuery(id+"F0.wireOp",EDGE,"E21.MirrorCS");var subQ2=makeQuery(id+"F0.imprint","INTERSECT",VERTEX,{"derivedFrom":[subQ1,subQ0]});Q65=makeQuery(id+"F0.imprint","IMPRINT",FACE,{"disambiguationData":[TD([[makeQuery(id+"F0.imprint","IMPRINT",EDGE,{"disambiguationData":[TD([[subQ2,-1.0]])],"derivedFrom":subQ1}),-1.0]])]});}
            var Q66;
            {var subQ0=sQuery(id+"F0.wireOp",EDGE,"E34.MirrorCS");var subQ1=sQuery(id+"F0.wireOp",EDGE,"E21.MirrorCS");var subQ2=makeQuery(id+"F0.imprint","INTERSECT",VERTEX,{"derivedFrom":[subQ1,subQ0]});Q66=makeQuery(id+"F0.imprint","IMPRINT",FACE,{"disambiguationData":[TD([[makeQuery(id+"F0.imprint","IMPRINT",EDGE,{"disambiguationData":[TD([[subQ2,-1.0]])],"derivedFrom":subQ1}),-1.0]])]});}
            var Q67;
            {var subQ0=sQuery(id+"F0.wireOp",EDGE,"E35.MirrorCS");var subQ1=sQuery(id+"F0.wireOp",EDGE,"E22.MirrorCS");var subQ2=makeQuery(id+"F0.imprint","INTERSECT",VERTEX,{"derivedFrom":[subQ1,subQ0]});Q67=makeQuery(id+"F0.imprint","IMPRINT",FACE,{"disambiguationData":[TD([[makeQuery(id+"F0.imprint","IMPRINT",EDGE,{"disambiguationData":[TD([[subQ2,-1.0]])],"derivedFrom":subQ1}),-1.0]])]});}
            var Q68;
            {var subQ3=sQuery(id+"F0.wireOp",EDGE,"E17");var subQ5=sQuery(id+"F0.wireOp",EDGE,"E6");var subQ6=makeQuery(id+"F0.imprint","INTERSECT",VERTEX,{"derivedFrom":[subQ5,subQ3]});Q68=makeQuery(id+"F0.imprint","IMPRINT",FACE,{"disambiguationData":[TD([[makeQuery(id+"F0.imprint","IMPRINT",EDGE,{"disambiguationData":[TD([[subQ6,-1.0]])],"derivedFrom":subQ5}),1.0]])]});}
            var Q69;
            {var subQ0=sQuery(id+"F0.wireOp",EDGE,"E17");var subQ1=sQuery(id+"F0.wireOp",EDGE,"E3");var subQ2=makeQuery(id+"F0.imprint","INTERSECT",VERTEX,{"derivedFrom":[subQ1,subQ0]});Q69=makeQuery(id+"F0.imprint","IMPRINT",FACE,{"disambiguationData":[TD([[makeQuery(id+"F0.imprint","IMPRINT",EDGE,{"disambiguationData":[TD([[subQ2,-1.0]])],"derivedFrom":subQ1}),-1.0]])]});}
            var Q70;
            {var subQ0=sQuery(id+"F0.wireOp",EDGE,"E17");var subQ1=sQuery(id+"F0.wireOp",EDGE,"E2");var subQ2=makeQuery(id+"F0.imprint","INTERSECT",VERTEX,{"derivedFrom":[subQ1,subQ0]});Q70=makeQuery(id+"F0.imprint","IMPRINT",FACE,{"disambiguationData":[TD([[makeQuery(id+"F0.imprint","IMPRINT",EDGE,{"disambiguationData":[TD([[subQ2,-1.0]])],"derivedFrom":subQ1}),-1.0]])]});}
            var Q71;
            {var subQ0=sQuery(id+"F0.wireOp",EDGE,"E35.MirrorCS");var subQ1=sQuery(id+"F0.wireOp",EDGE,"E24.MirrorCS");var subQ2=makeQuery(id+"F0.imprint","INTERSECT",VERTEX,{"derivedFrom":[subQ1,subQ0]});Q71=makeQuery(id+"F0.imprint","IMPRINT",FACE,{"disambiguationData":[TD([[makeQuery(id+"F0.imprint","IMPRINT",EDGE,{"disambiguationData":[TD([[subQ2,-1.0]])],"derivedFrom":subQ1}),-1.0]])]});}
            extrude(context, id + "F1", {"entities" : qUnion([Q0, Q1, Q2, Q3, Q4, Q5, Q6, Q7, Q8, Q9, Q10, Q11, Q12, Q13, Q14, Q15, Q16, Q17, Q18, Q19, Q20, Q21, Q22, Q23, Q24, Q25, Q26, Q27, Q28, Q29, Q30, Q31, Q32, Q33, Q34, Q35, Q36, Q37, Q38, Q39, Q40, Q41, Q42, Q43, Q44, Q45, Q46, Q47, Q48, Q49, Q50, Q51, Q52, Q53, Q54, Q55, Q56, Q57, Q58, Q59, Q60, Q61, Q62, Q63, Q64, Q65, Q66, Q67, Q68, Q69, Q70, Q71]), "depth" : 25.4 * mm});
        }
        {
            var Q0;
            Q0=qCreatedBy(makeId("Front.planeOp"),FACE);
            var sketch = newSketch(context, id + "F2", { "sketchPlane" : qUnion([Q0])});
            skLineSegment(sketch, "E37.bottom", {"start": v(-42.42, 30.83) * mm, "end": v(-34.3, 30.83) * mm});
            skLineSegment(sketch, "E37.top", {"start": v(-42.42, 38.59) * mm, "end": v(-34.3, 38.59) * mm});
            skLineSegment(sketch, "E37.left", {"start": v(-42.42, 30.83) * mm, "end": v(-42.42, 38.59) * mm});
            skLineSegment(sketch, "E37.right", {"start": v(-34.3, 30.83) * mm, "end": v(-34.3, 38.59) * mm});
            skLineSegment(sketch, "E38.2.0.0", {"start": v(8.38, 30.83) * mm, "end": v(8.38, 38.59) * mm});
            skLineSegment(sketch, "E38.2.0.1", {"start": v(8.38, 38.59) * mm, "end": v(16.5, 38.59) * mm});
            skLineSegment(sketch, "E38.2.0.2", {"start": v(16.5, 30.83) * mm, "end": v(16.5, 38.59) * mm});
            skLineSegment(sketch, "E38.2.0.3", {"start": v(8.38, 30.83) * mm, "end": v(16.5, 30.83) * mm});
            skLineSegment(sketch, "E39.bottom", {"start": v(-25.4, 38.59) * mm, "end": v(-16.76, 38.59) * mm});
            skLineSegment(sketch, "E39.top", {"start": v(-25.4, 30.73) * mm, "end": v(-16.76, 30.73) * mm});
            skLineSegment(sketch, "E39.left", {"start": v(-25.4, 38.59) * mm, "end": v(-25.4, 30.73) * mm});
            skLineSegment(sketch, "E39.right", {"start": v(-16.76, 38.59) * mm, "end": v(-16.76, 30.73) * mm});
            skLineSegment(sketch, "E40.bottom", {"start": v(-8.9, 38.59) * mm, "end": v(0, 38.59) * mm});
            skLineSegment(sketch, "E40.top", {"start": v(-8.9, 30.73) * mm, "end": v(0, 30.73) * mm});
            skLineSegment(sketch, "E40.left", {"start": v(-8.9, 38.59) * mm, "end": v(-8.9, 30.73) * mm});
            skLineSegment(sketch, "E40.right", {"start": v(0, 38.59) * mm, "end": v(0, 30.73) * mm});
            skPoint(sketch, "E41.oppositeSnap0", {"position": v(-4.45, 30.73) * mm});
            skLineSegment(sketch, "E41.bottom", {"start": v(25.4, 38.59) * mm, "end": v(34.04, 38.59) * mm});
            skLineSegment(sketch, "E41.top", {"start": v(25.4, 30.73) * mm, "end": v(34.04, 30.73) * mm});
            skLineSegment(sketch, "E41.left", {"start": v(25.4, 38.59) * mm, "end": v(25.4, 30.73) * mm});
            skLineSegment(sketch, "E41.right", {"start": v(34.04, 38.59) * mm, "end": v(34.04, 30.73) * mm});
            skSolve(sketch);
        }
        {
            var Q0;
            Q0=makeQuery(id+"F2.imprint","IMPRINT",FACE,{"disambiguationData":[TD([[makeQuery(id+"F2.imprint","IMPRINT",EDGE,{"derivedFrom":sQuery(id+"F2.wireOp",EDGE,"E40.bottom")}),-1.0]])]});
            var Q1;
            Q1=makeQuery(id+"F2.imprint","IMPRINT",FACE,{"disambiguationData":[TD([[makeQuery(id+"F2.imprint","IMPRINT",EDGE,{"derivedFrom":sQuery(id+"F2.wireOp",EDGE,"E39.bottom")}),-1.0]])]});
            var Q2;
            Q2=makeQuery(id+"F2.imprint","IMPRINT",FACE,{"disambiguationData":[TD([[makeQuery(id+"F2.imprint","IMPRINT",EDGE,{"derivedFrom":sQuery(id+"F2.wireOp",EDGE,"E38.2.0.0")}),-1.0]])]});
            var Q3;
            Q3=makeQuery(id+"F2.imprint","IMPRINT",FACE,{"disambiguationData":[TD([[makeQuery(id+"F2.imprint","IMPRINT",EDGE,{"derivedFrom":sQuery(id+"F2.wireOp",EDGE,"E37.bottom")}),1.0]])]});
            var Q4;
            Q4=makeQuery(id+"F2.imprint","IMPRINT",FACE,{"disambiguationData":[TD([[makeQuery(id+"F2.imprint","IMPRINT",EDGE,{"derivedFrom":sQuery(id+"F2.wireOp",EDGE,"E41.bottom")}),-1.0]])]});
            extrude(context, id + "F3", {"entities" : qUnion([Q0, Q1, Q2, Q3, Q4]), "depth" : 25.4 * mm});
        }
    });
